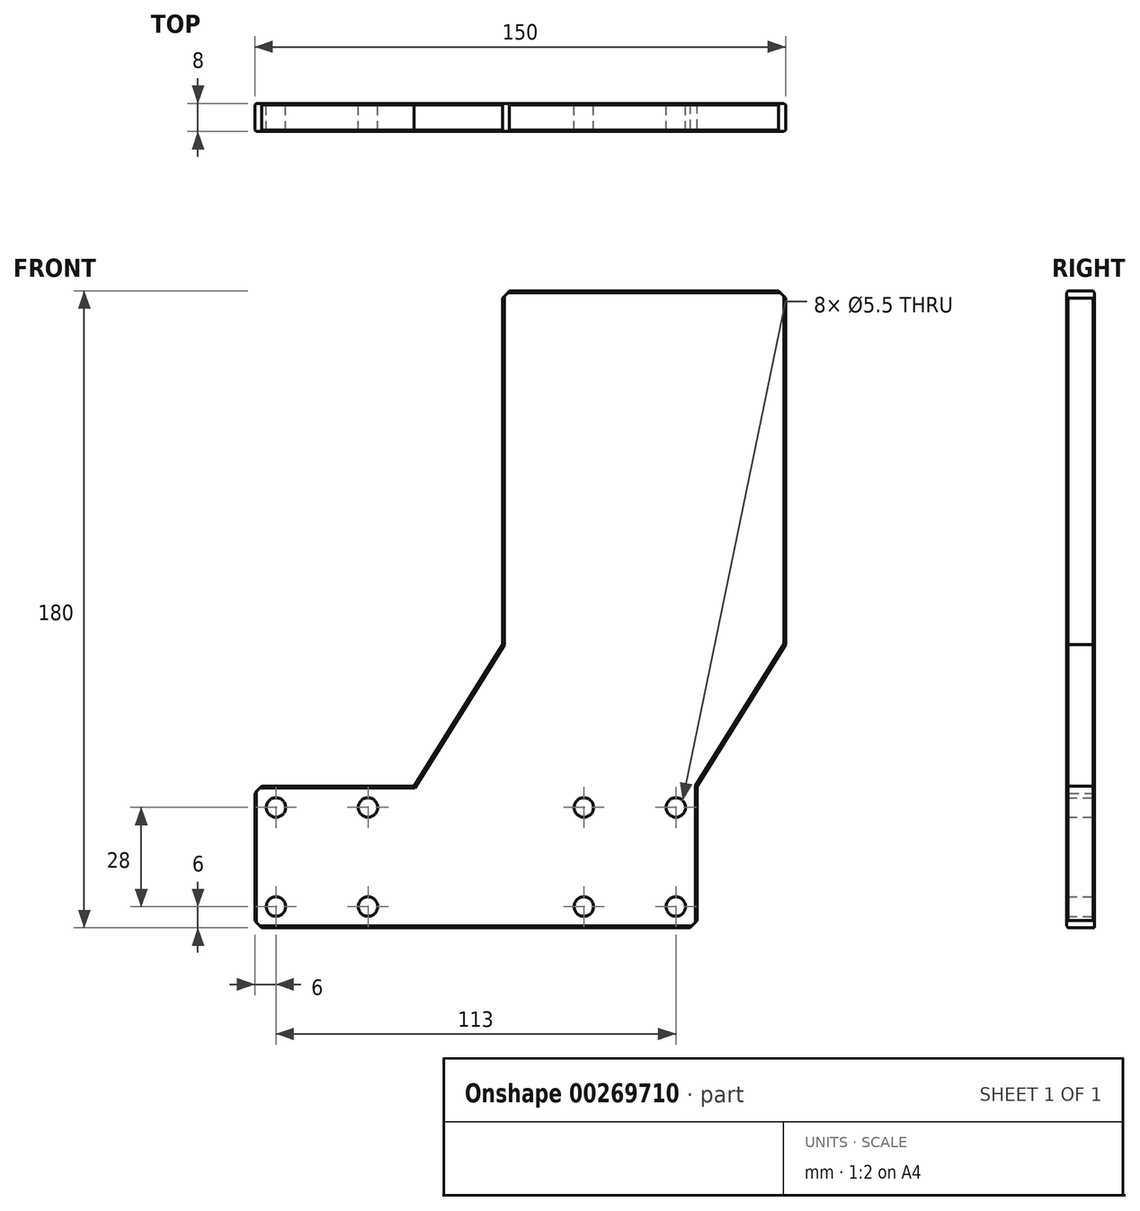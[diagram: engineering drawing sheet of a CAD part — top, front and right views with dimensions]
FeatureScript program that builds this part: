
annotation { "Feature Type Name" : "Feature", "Feature Type Description" : "" }
export const myFeature = defineFeature(function(context is Context, id is Id, definition is map)
    precondition{}
    {
        {
            var Q0;
            Q0=qCreatedBy(makeId("Front.planeOp"),FACE);
            var sketch = newSketch(context, id + "F0", { "sketchPlane" : qUnion([Q0])});
            skLineSegment(sketch, "E0.bottom", {"start": v(70, 180) * mm, "end": v(150, 180) * mm});
            skLineSegment(sketch, "E0.top", {"start": v(70, 80) * mm, "end": v(150, 80) * mm, "construction": true});
            skLineSegment(sketch, "E0.left", {"start": v(70, 180) * mm, "end": v(70, 80) * mm});
            skLineSegment(sketch, "E0.right", {"start": v(150, 180) * mm, "end": v(150, 80) * mm});
            skLineSegment(sketch, "E1.bottom", {"start": v(0, 40) * mm, "end": v(45, 40) * mm});
            skLineSegment(sketch, "E1.top", {"start": v(0, 0) * mm, "end": v(125, 0) * mm});
            skLineSegment(sketch, "E1.left", {"start": v(0, 40) * mm, "end": v(0, 0) * mm});
            skLineSegment(sketch, "E1.right", {"start": v(125, 40) * mm, "end": v(125, 0) * mm});
            skLineSegment(sketch, "E2", {"start": v(150, 80) * mm, "end": v(125, 40) * mm});
            skLineSegment(sketch, "E3", {"start": v(70, 80) * mm, "end": v(45, 40) * mm});
            skSolve(sketch);
        }
        {
            var Q0;
            Q0=makeQuery(id+"F0.imprint","IMPRINT",FACE,{"disambiguationData":[TD([[makeQuery(id+"F0.imprint","IMPRINT",EDGE,{"derivedFrom":sQuery(id+"F0.wireOp",EDGE,"E0.bottom")}),-1.0]])]});
            extrude(context, id + "F1", {"entities" : qUnion([Q0]), "depth" : 8 * mm});
        }
        {
            var Q0;
            Q0=makeQuery(id+"F1.opExtrude","CAP_FACE",FACE,{"disambiguationData":[OSD([sQuery(id+"F0.wireOp",EDGE,"E0.bottom"),sQuery(id+"F0.wireOp",EDGE,"E0.left"),sQuery(id+"F0.wireOp",EDGE,"E0.right"),sQuery(id+"F0.wireOp",EDGE,"E1.bottom"),sQuery(id+"F0.wireOp",EDGE,"E1.top"),sQuery(id+"F0.wireOp",EDGE,"E1.left"),sQuery(id+"F0.wireOp",EDGE,"E1.right"),sQuery(id+"F0.wireOp",EDGE,"E2"),sQuery(id+"F0.wireOp",EDGE,"E3")])],"isStart":false});
            var sketch = newSketch(context, id + "F2", { "sketchPlane" : qUnion([Q0])});
            skLineSegment(sketch, "E4", {"start": v(0, 20) * mm, "end": v(150.95, 20) * mm, "construction": true});
            skLineSegment(sketch, "E5", {"start": v(-11.77, 34) * mm, "end": v(158.4, 34) * mm, "construction": true});
            skLineSegment(sketch, "E6", {"start": v(-11.45, 6) * mm, "end": v(159.06, 6) * mm, "construction": true});
            skLineSegment(sketch, "E7", {"start": v(62.5, 0) * mm, "end": v(62.5, 40) * mm, "construction": true});
            skPoint(sketch, "E7.endSnap0", {"position": v(22.5, 40) * mm});
            skLineSegment(sketch, "E8", {"start": v(6, 36.94) * mm, "end": v(6, 2.9) * mm, "construction": true});
            skLineSegment(sketch, "E9", {"start": v(119, 38.89) * mm, "end": v(119, 3.23) * mm, "construction": true});
            skLineSegment(sketch, "E10", {"start": v(93, 39.53) * mm, "end": v(93, 2.9) * mm, "construction": true});
            skLineSegment(sketch, "E11", {"start": v(32, 36.3) * mm, "end": v(32, 4.2) * mm, "construction": true});
            skPoint(sketch, "E12", {"position": v(6, 34) * mm});
            skPoint(sketch, "E13", {"position": v(32, 34) * mm});
            skPoint(sketch, "E14", {"position": v(6, 6) * mm});
            skPoint(sketch, "E15", {"position": v(32, 6) * mm});
            skPoint(sketch, "E16", {"position": v(119, 6) * mm});
            skPoint(sketch, "E17", {"position": v(93, 6) * mm});
            skPoint(sketch, "E18", {"position": v(93, 34) * mm});
            skPoint(sketch, "E19", {"position": v(119, 34) * mm});
            skSolve(sketch);
        }
        {
            var Q0;
            Q0=sQuery(id+"F2.wireOp",VERTEX,"E18");
            var Q1;
            Q1=sQuery(id+"F2.wireOp",VERTEX,"E12");
            var Q2;
            Q2=sQuery(id+"F2.wireOp",VERTEX,"E13");
            var Q3;
            Q3=sQuery(id+"F2.wireOp",VERTEX,"E19");
            var Q4;
            Q4=sQuery(id+"F2.wireOp",VERTEX,"E16");
            var Q5;
            Q5=sQuery(id+"F2.wireOp",VERTEX,"E17");
            var Q6;
            Q6=sQuery(id+"F2.wireOp",VERTEX,"E15");
            var Q7;
            Q7=sQuery(id+"F2.wireOp",VERTEX,"E14");
            var Q8;
            Q8=makeQuery(id+"F1.opExtrude","SWEPT_BODY",BODY,{"disambiguationData":[OSD([sQuery(id+"F0.wireOp",EDGE,"E0.bottom"),sQuery(id+"F0.wireOp",EDGE,"E0.left"),sQuery(id+"F0.wireOp",EDGE,"E0.right"),sQuery(id+"F0.wireOp",EDGE,"E1.bottom"),sQuery(id+"F0.wireOp",EDGE,"E1.top"),sQuery(id+"F0.wireOp",EDGE,"E1.left"),sQuery(id+"F0.wireOp",EDGE,"E1.right"),sQuery(id+"F0.wireOp",EDGE,"E2"),sQuery(id+"F0.wireOp",EDGE,"E3")])]});
            hole(context, id + "F3", {"style" : HoleStyle.SIMPLE, "endStyle" : HoleEndStyle.THROUGH, "holeDiameter" : 5.5 * mm, "locations" : qUnion([Q0, Q1, Q2, Q3, Q4, Q5, Q6, Q7]), "scope" : qUnion([Q8]), "isTappedThrough" : true, "startStyle" : HoleStartStyle.PART});
        }
        {
            var Q0;
            Q0=makeQuery(id+"F1.opExtrude","CAP_EDGE",EDGE,{"disambiguationData":[OSD([sQuery(id+"F0.wireOp",EDGE,"E0.bottom")])],"isStart":false});
            var Q1;
            Q1=makeQuery(id+"F1.opExtrude","CAP_EDGE",EDGE,{"disambiguationData":[OSD([sQuery(id+"F0.wireOp",EDGE,"E0.left")])],"isStart":false});
            var Q2;
            Q2=makeQuery(id+"F1.opExtrude","CAP_EDGE",EDGE,{"disambiguationData":[OSD([sQuery(id+"F0.wireOp",EDGE,"E3")])],"isStart":false});
            var Q3;
            Q3=makeQuery(id+"F1.opExtrude","CAP_EDGE",EDGE,{"disambiguationData":[OSD([sQuery(id+"F0.wireOp",EDGE,"E1.bottom")])],"isStart":false});
            var Q4;
            Q4=makeQuery(id+"F1.opExtrude","CAP_EDGE",EDGE,{"disambiguationData":[OSD([sQuery(id+"F0.wireOp",EDGE,"E1.left")])],"isStart":false});
            var Q5;
            Q5=makeQuery(id+"F1.opExtrude","CAP_EDGE",EDGE,{"disambiguationData":[OSD([sQuery(id+"F0.wireOp",EDGE,"E1.top")])],"isStart":false});
            var Q6;
            Q6=makeQuery(id+"F1.opExtrude","CAP_EDGE",EDGE,{"disambiguationData":[OSD([sQuery(id+"F0.wireOp",EDGE,"E1.right")])],"isStart":false});
            var Q7;
            Q7=makeQuery(id+"F1.opExtrude","CAP_EDGE",EDGE,{"disambiguationData":[OSD([sQuery(id+"F0.wireOp",EDGE,"E2")])],"isStart":false});
            var Q8;
            Q8=makeQuery(id+"F1.opExtrude","CAP_EDGE",EDGE,{"disambiguationData":[OSD([sQuery(id+"F0.wireOp",EDGE,"E0.right")])],"isStart":false});
            var Q9;
            Q9=makeQuery(id+"F1.opExtrude","CAP_EDGE",EDGE,{"disambiguationData":[OSD([sQuery(id+"F0.wireOp",EDGE,"E0.bottom")])],"isStart":true});
            var Q10;
            Q10=makeQuery(id+"F1.opExtrude","CAP_EDGE",EDGE,{"disambiguationData":[OSD([sQuery(id+"F0.wireOp",EDGE,"E0.right")])],"isStart":true});
            var Q11;
            Q11=makeQuery(id+"F1.opExtrude","CAP_EDGE",EDGE,{"disambiguationData":[OSD([sQuery(id+"F0.wireOp",EDGE,"E2")])],"isStart":true});
            var Q12;
            Q12=makeQuery(id+"F1.opExtrude","CAP_EDGE",EDGE,{"disambiguationData":[OSD([sQuery(id+"F0.wireOp",EDGE,"E1.right")])],"isStart":true});
            var Q13;
            Q13=makeQuery(id+"F1.opExtrude","CAP_EDGE",EDGE,{"disambiguationData":[OSD([sQuery(id+"F0.wireOp",EDGE,"E1.left")])],"isStart":true});
            var Q14;
            Q14=makeQuery(id+"F1.opExtrude","CAP_EDGE",EDGE,{"disambiguationData":[OSD([sQuery(id+"F0.wireOp",EDGE,"E1.bottom")])],"isStart":true});
            var Q15;
            Q15=makeQuery(id+"F1.opExtrude","CAP_EDGE",EDGE,{"disambiguationData":[OSD([sQuery(id+"F0.wireOp",EDGE,"E3")])],"isStart":true});
            var Q16;
            Q16=makeQuery(id+"F1.opExtrude","CAP_EDGE",EDGE,{"disambiguationData":[OSD([sQuery(id+"F0.wireOp",EDGE,"E0.left")])],"isStart":true});
            chamfer(context, id + "F4", {"entities" : qUnion([Q0, Q1, Q2, Q3, Q4, Q5, Q6, Q7, Q8, Q9, Q10, Q11, Q12, Q13, Q14, Q15, Q16]), "width" : 0.5 * mm, "tangentPropagation" : true});
        }
        {
            var Q0;
            Q0=makeQuery(id+"F1.opExtrude","SWEPT_EDGE",EDGE,{"disambiguationData":[OSD([sQuery(id+"F0.wireOp",EDGE,"E0.bottom"),sQuery(id+"F0.wireOp",EDGE,"E0.left")])]});
            var Q1;
            Q1=makeQuery(id+"F1.opExtrude","SWEPT_EDGE",EDGE,{"disambiguationData":[OSD([sQuery(id+"F0.wireOp",EDGE,"E0.bottom"),sQuery(id+"F0.wireOp",EDGE,"E0.right")])]});
            var Q2;
            Q2=makeQuery(id+"F1.opExtrude","SWEPT_EDGE",EDGE,{"disambiguationData":[OSD([sQuery(id+"F0.wireOp",EDGE,"E1.bottom"),sQuery(id+"F0.wireOp",EDGE,"E1.left")])]});
            var Q3;
            Q3=makeQuery(id+"F1.opExtrude","SWEPT_EDGE",EDGE,{"disambiguationData":[OSD([sQuery(id+"F0.wireOp",EDGE,"E1.top"),sQuery(id+"F0.wireOp",EDGE,"E1.left")])]});
            var Q4;
            Q4=makeQuery(id+"F1.opExtrude","SWEPT_EDGE",EDGE,{"disambiguationData":[OSD([sQuery(id+"F0.wireOp",EDGE,"E1.top"),sQuery(id+"F0.wireOp",EDGE,"E1.right")])]});
            chamfer(context, id + "F5", {"entities" : qUnion([Q0, Q1, Q2, Q3, Q4]), "width" : 2 * mm, "tangentPropagation" : true});
        }
    });
